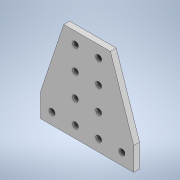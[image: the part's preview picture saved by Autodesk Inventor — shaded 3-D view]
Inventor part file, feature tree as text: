
AUTODESK INVENTOR PART (.ipt)
format: ipt  version: 2020 (Build 240168000, 168)  size: 124,416 bytes
history: native  units: in
note: dims shown in document units (in); Inventor stores cm internally (conversion verified against a paired STEP export)
features: extrude x1, sketch x1
ambient origin geometry x8: Origin, YZ Plane, XZ Plane, XY Plane, X Axis, Y Axis, Z Axis, Center Point
bodies: Solid1 (feature_tree)
feature tree (2):
  extrude  "Extrusion1"  Depth=4.0in
  sketch  "Sketch1"  dims[d0=4.0in d1=4.0in d2=1.0in d3=1.0in d4=0.256in d5=0.5in d6=0.5in d7=1.5748in d9=1.0in d10=0.3937in d12=1.0in d14=1.5748in d16=1.0in d17=0.3937in d19=1.0in d21=1.0in d22=1.0in d23=0.25in d24=0.0in]
